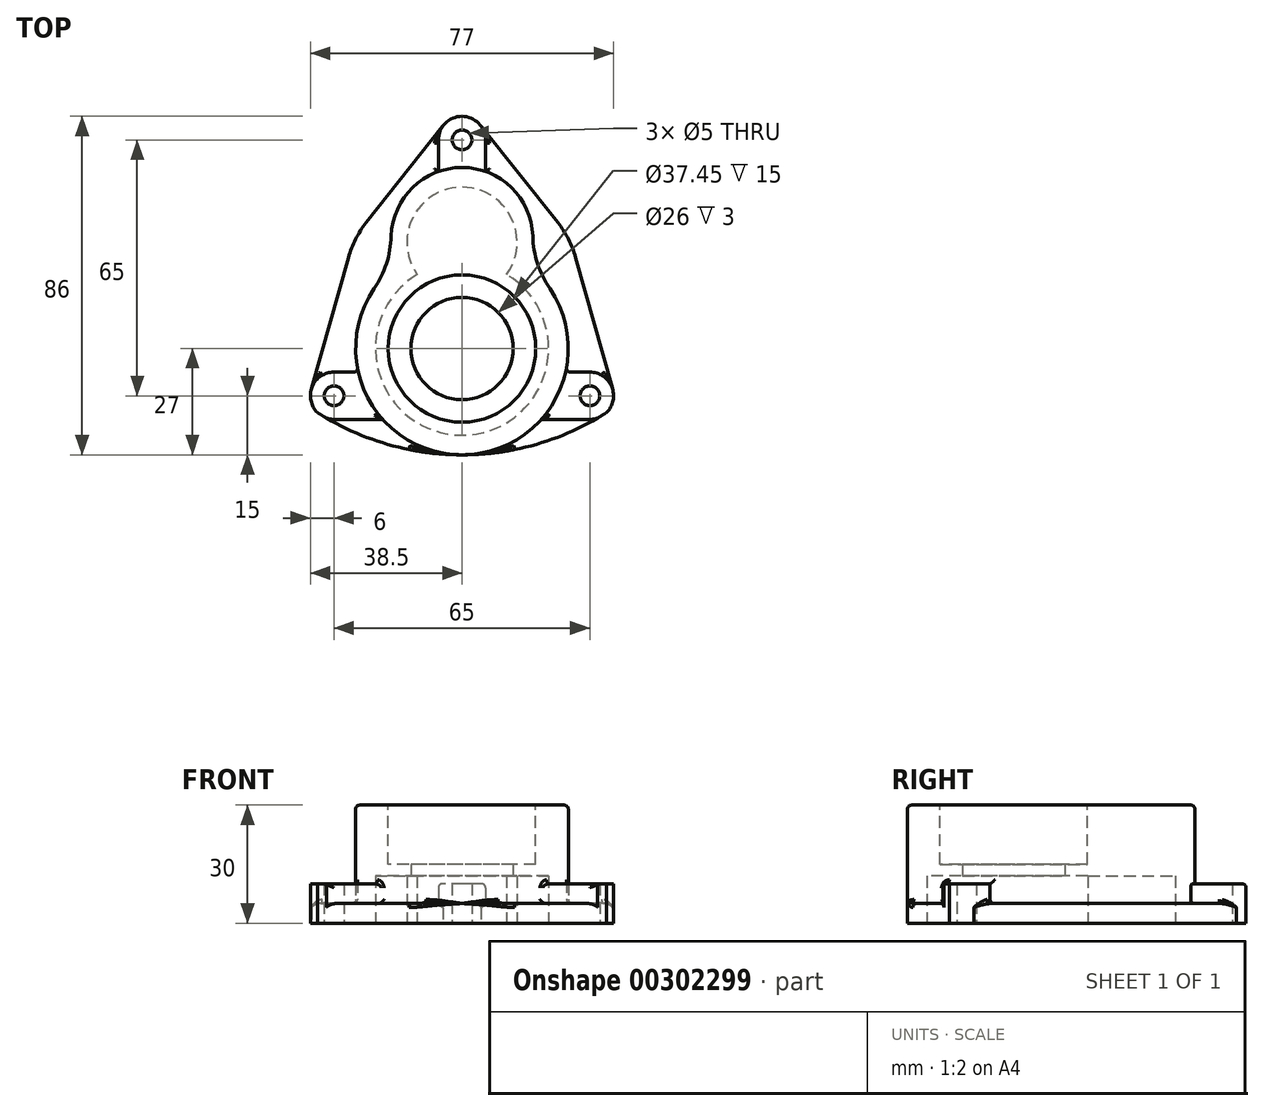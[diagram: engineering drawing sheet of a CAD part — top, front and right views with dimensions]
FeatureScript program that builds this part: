
annotation { "Feature Type Name" : "Feature", "Feature Type Description" : "" }
export const myFeature = defineFeature(function(context is Context, id is Id, definition is map)
    precondition{}
    {
        {
            var Q0;
            Q0=qCreatedBy(makeId("Top.planeOp"),FACE);
            var sketch = newSketch(context, id + "F0", { "sketchPlane" : qUnion([Q0])});
            skCircle(sketch, "E0", {"center": v(0, 0) * mm, "radius": 13 * mm});
            skCircle(sketch, "E1", {"center": v(0, 0) * mm, "radius": 22 * mm});
            skCircle(sketch, "E2", {"center": v(0, 53) * mm, "radius": 2.5 * mm});
            skCircle(sketch, "E3", {"center": v(0, 53) * mm, "radius": 6 * mm});
            skCircle(sketch, "E4", {"center": v(32.5, -12) * mm, "radius": 2.5 * mm});
            skCircle(sketch, "E5", {"center": v(32.5, -12) * mm, "radius": 6 * mm});
            skCircle(sketch, "E6", {"center": v(-32.5, -12) * mm, "radius": 2.5 * mm});
            skCircle(sketch, "E7", {"center": v(-32.5, -12) * mm, "radius": 6 * mm});
            skCircle(sketch, "E8", {"center": v(0, 27) * mm, "radius": 14 * mm});
            skLineSegment(sketch, "E9", {"start": v(32.5, -18) * mm, "end": v(20.12, -18) * mm});
            skLineSegment(sketch, "E10", {"start": v(32.5, -6) * mm, "end": v(26.32, -6) * mm});
            skLineSegment(sketch, "E11", {"start": v(-32.5, -6) * mm, "end": v(-26.32, -6) * mm});
            skLineSegment(sketch, "E12", {"start": v(-32.5, -18) * mm, "end": v(-20.12, -18) * mm});
            skLineSegment(sketch, "E13", {"start": v(-6, 53) * mm, "end": v(-6, 44.97) * mm});
            skLineSegment(sketch, "E14", {"start": v(6, 53) * mm, "end": v(6, 44.97) * mm});
            skLineSegment(sketch, "E15", {"start": v(4.87, 56.5) * mm, "end": v(24.37, 31.94) * mm});
            skLineSegment(sketch, "E16", {"start": v(-4.87, 56.5) * mm, "end": v(-24.37, 31.94) * mm});
            skLineSegment(sketch, "E17", {"start": v(-38.18, -10.07) * mm, "end": v(-28.86, 23.15) * mm});
            skLineSegment(sketch, "E18", {"start": v(38.18, -10.07) * mm, "end": v(28.86, 23.15) * mm});
            skArc(sketch, "E19", {"start": v(-36.7, -16.28) * mm, "mid": v(0, -27) * mm, "end": v(36.7, -16.28) * mm});
            skPoint(sketch, "E20.visualSharp", {"position": v(27.5, 28) * mm});
            skArc(sketch, "E20.filletArc", {"start": v(28.86, 23.15) * mm, "mid": v(27.05, 27.77) * mm, "end": v(24.37, 31.94) * mm});
            skPoint(sketch, "E21.visualSharp", {"position": v(-27.5, 28) * mm});
            skArc(sketch, "E21.filletArc", {"start": v(-24.37, 31.94) * mm, "mid": v(-27.05, 27.77) * mm, "end": v(-28.86, 23.15) * mm});
            skArc(sketch, "E22", {"start": v(16.68, 21.23) * mm, "mid": v(0, 46) * mm, "end": v(-16.68, 21.23) * mm});
            skArc(sketch, "E23", {"start": v(-16.68, 21.23) * mm, "mid": v(0, -27) * mm, "end": v(16.68, 21.23) * mm});
            skCircle(sketch, "E24", {"center": v(0, 0) * mm, "radius": 18.73 * mm});
            skSolve(sketch);
        }
        {
            var Q0;
            {var subQ3=sQuery(id+"F0.wireOp",EDGE,"E8");var subQ4=sQuery(id+"F0.wireOp",EDGE,"E1");var subQ5=makeQuery(id+"F0.imprint","INTERSECT",VERTEX,{"disambiguationData":[OD(0.0)],"derivedFrom":[subQ4,subQ3]});Q0=makeQuery(id+"F0.imprint","IMPRINT",FACE,{"disambiguationData":[TD([[makeQuery(id+"F0.imprint","IMPRINT",EDGE,{"disambiguationData":[TD([[subQ5,-1.0]])],"derivedFrom":subQ4}),-1.0]])]});}
            var Q1;
            {var subQ0=sQuery(id+"F0.wireOp",EDGE,"E8");var subQ1=sQuery(id+"F0.wireOp",EDGE,"E1");var subQ2=makeQuery(id+"F0.imprint","INTERSECT",VERTEX,{"disambiguationData":[OD(0.0)],"derivedFrom":[subQ1,subQ0]});Q1=makeQuery(id+"F0.imprint","IMPRINT",FACE,{"disambiguationData":[TD([[makeQuery(id+"F0.imprint","IMPRINT",EDGE,{"disambiguationData":[TD([[subQ2,1.0]])],"derivedFrom":subQ1}),-1.0]])]});}
            var Q2;
            {var subQ0=sQuery(id+"F0.wireOp",EDGE,"E8");var subQ1=sQuery(id+"F0.wireOp",EDGE,"E1");var subQ2=makeQuery(id+"F0.imprint","INTERSECT",VERTEX,{"disambiguationData":[OD(0.0)],"derivedFrom":[subQ1,subQ0]});Q2=makeQuery(id+"F0.imprint","IMPRINT",FACE,{"disambiguationData":[TD([[makeQuery(id+"F0.imprint","IMPRINT",EDGE,{"disambiguationData":[TD([[subQ2,1.0]])],"derivedFrom":subQ1}),1.0]])]});}
            var Q3;
            {var subQ0=sQuery(id+"F0.wireOp",EDGE,"E8");var subQ1=makeQuery(id+"F0.imprint","INTERSECT",VERTEX,{"derivedFrom":[sQuery(id+"F0.wireOp",EDGE,"E0"),subQ0]});Q3=makeQuery(id+"F0.imprint","IMPRINT",FACE,{"disambiguationData":[TD([[makeQuery(id+"F0.imprint","IMPRINT",EDGE,{"disambiguationData":[TD([[subQ1,1.0]])],"derivedFrom":subQ0}),1.0]])]});}
            var Q4;
            Q4=makeQuery(id+"F0.imprint","IMPRINT",FACE,{"disambiguationData":[TD([[makeQuery(id+"F0.imprint","IMPRINT",EDGE,{"derivedFrom":sQuery(id+"F0.wireOp",EDGE,"E0")}),1.0]])]});
            var Q5;
            {var subQ0=sQuery(id+"F0.wireOp",EDGE,"E0");Q5=makeQuery(id+"F0.imprint","IMPRINT",FACE,{"disambiguationData":[TD([[makeQuery(id+"F0.imprint","IMPRINT",EDGE,{"derivedFrom":subQ0}),-1.0]])]});}
            var Q6;
            {var subQ0=sQuery(id+"F0.wireOp",EDGE,"E8");var subQ1=sQuery(id+"F0.wireOp",EDGE,"E1");var subQ2=makeQuery(id+"F0.imprint","INTERSECT",VERTEX,{"disambiguationData":[OD(0.0)],"derivedFrom":[subQ1,subQ0]});Q6=makeQuery(id+"F0.imprint","IMPRINT",FACE,{"disambiguationData":[TD([[makeQuery(id+"F0.imprint","IMPRINT",EDGE,{"disambiguationData":[TD([[subQ2,-1.0]])],"derivedFrom":subQ1}),1.0]])]});}
            extrude(context, id + "F1", {"entities" : qUnion([Q0, Q1, Q2, Q3, Q4, Q5, Q6]), "depth" : 30 * mm});
        }
        {
            var Q0;
            Q0=makeQuery(id+"F0.imprint","IMPRINT",FACE,{"disambiguationData":[TD([[makeQuery(id+"F0.imprint","IMPRINT",EDGE,{"derivedFrom":sQuery(id+"F0.wireOp",EDGE,"E2")}),-1.0]])]});
            var Q1;
            {var subQ0=sQuery(id+"F0.wireOp",EDGE,"E13");Q1=makeQuery(id+"F0.imprint","IMPRINT",FACE,{"disambiguationData":[TD([[makeQuery(id+"F0.imprint","IMPRINT",EDGE,{"derivedFrom":subQ0}),1.0]])]});}
            var Q2;
            Q2=makeQuery(id+"F0.imprint","IMPRINT",FACE,{"disambiguationData":[TD([[makeQuery(id+"F0.imprint","IMPRINT",EDGE,{"derivedFrom":sQuery(id+"F0.wireOp",EDGE,"E4")}),-1.0]])]});
            var Q3;
            {var subQ0=sQuery(id+"F0.wireOp",EDGE,"E9");Q3=makeQuery(id+"F0.imprint","IMPRINT",FACE,{"disambiguationData":[TD([[makeQuery(id+"F0.imprint","IMPRINT",EDGE,{"derivedFrom":subQ0}),-1.0]])]});}
            var Q4;
            {var subQ0=sQuery(id+"F0.wireOp",EDGE,"E11");Q4=makeQuery(id+"F0.imprint","IMPRINT",FACE,{"disambiguationData":[TD([[makeQuery(id+"F0.imprint","IMPRINT",EDGE,{"derivedFrom":subQ0}),-1.0]])]});}
            var Q5;
            Q5=makeQuery(id+"F0.imprint","IMPRINT",FACE,{"disambiguationData":[TD([[makeQuery(id+"F0.imprint","IMPRINT",EDGE,{"derivedFrom":sQuery(id+"F0.wireOp",EDGE,"E6")}),-1.0]])]});
            extrude(context, id + "F2", {"entities" : qUnion([Q0, Q1, Q2, Q3, Q4, Q5]), "operationType" : NewBodyOperationType.ADD, "depth" : 10 * mm});
        }
        {
            var Q0;
            {var subQ1=sQuery(id+"F0.wireOp",EDGE,"E11");Q0=makeQuery(id+"F0.imprint","IMPRINT",FACE,{"disambiguationData":[TD([[makeQuery(id+"F0.imprint","IMPRINT",EDGE,{"derivedFrom":subQ1}),1.0]])]});}
            var Q1;
            {var subQ4=sQuery(id+"F0.wireOp",EDGE,"E10");Q1=makeQuery(id+"F0.imprint","IMPRINT",FACE,{"disambiguationData":[TD([[makeQuery(id+"F0.imprint","IMPRINT",EDGE,{"derivedFrom":subQ4}),-1.0]])]});}
            var Q2;
            {var subQ0=sQuery(id+"F0.wireOp",EDGE,"E9");Q2=makeQuery(id+"F0.imprint","IMPRINT",FACE,{"disambiguationData":[TD([[makeQuery(id+"F0.imprint","IMPRINT",EDGE,{"derivedFrom":subQ0}),1.0]])]});}
            var Q3;
            {var subQ0=sQuery(id+"F0.wireOp",EDGE,"E12");Q3=makeQuery(id+"F0.imprint","IMPRINT",FACE,{"disambiguationData":[TD([[makeQuery(id+"F0.imprint","IMPRINT",EDGE,{"derivedFrom":subQ0}),-1.0]])]});}
            extrude(context, id + "F3", {"entities" : qUnion([Q0, Q1, Q2, Q3]), "operationType" : NewBodyOperationType.ADD, "depth" : 5 * mm});
        }
        {
            var Q0;
            {var subQ0=sQuery(id+"F0.wireOp",EDGE,"E23");var subQ1=sQuery(id+"F0.wireOp",EDGE,"E22");Q0=makeQuery(id+"F1.opExtrude","SWEPT_EDGE",EDGE,{"disambiguationData":[OSD([subQ1,subQ0]),TDD([makeQuery(id+"F0.imprint","INTERSECT",VERTEX,{"disambiguationData":[OD(1.0)],"derivedFrom":[subQ1,subQ0]})])]});}
            var Q1;
            {var subQ0=sQuery(id+"F0.wireOp",EDGE,"E23");var subQ1=sQuery(id+"F0.wireOp",EDGE,"E22");Q1=makeQuery(id+"F1.opExtrude","SWEPT_EDGE",EDGE,{"disambiguationData":[OSD([subQ1,subQ0]),TDD([makeQuery(id+"F0.imprint","INTERSECT",VERTEX,{"disambiguationData":[OD(0.0)],"derivedFrom":[subQ1,subQ0]})])]});}
            fillet(context, id + "F4", {"entities" : qUnion([Q0, Q1]), "radius" : 25 * mm, "tangentPropagation" : true, "allowEdgeOverflow" : false});
        }
        {
            var Q0;
            {var subQ0=sQuery(id+"F0.wireOp",EDGE,"E8");var subQ1=sQuery(id+"F0.wireOp",EDGE,"E1");var subQ2=makeQuery(id+"F0.imprint","INTERSECT",VERTEX,{"disambiguationData":[OD(0.0)],"derivedFrom":[subQ1,subQ0]});Q0=makeQuery(id+"F0.imprint","IMPRINT",FACE,{"disambiguationData":[TD([[makeQuery(id+"F0.imprint","IMPRINT",EDGE,{"disambiguationData":[TD([[subQ2,1.0]])],"derivedFrom":subQ1}),-1.0]])]});}
            var Q1;
            {var subQ0=sQuery(id+"F0.wireOp",EDGE,"E8");var subQ1=sQuery(id+"F0.wireOp",EDGE,"E1");var subQ2=makeQuery(id+"F0.imprint","INTERSECT",VERTEX,{"disambiguationData":[OD(0.0)],"derivedFrom":[subQ1,subQ0]});Q1=makeQuery(id+"F0.imprint","IMPRINT",FACE,{"disambiguationData":[TD([[makeQuery(id+"F0.imprint","IMPRINT",EDGE,{"disambiguationData":[TD([[subQ2,1.0]])],"derivedFrom":subQ1}),1.0]])]});}
            var Q2;
            {var subQ0=sQuery(id+"F0.wireOp",EDGE,"E8");var subQ1=makeQuery(id+"F0.imprint","INTERSECT",VERTEX,{"derivedFrom":[sQuery(id+"F0.wireOp",EDGE,"E0"),subQ0]});Q2=makeQuery(id+"F0.imprint","IMPRINT",FACE,{"disambiguationData":[TD([[makeQuery(id+"F0.imprint","IMPRINT",EDGE,{"disambiguationData":[TD([[subQ1,1.0]])],"derivedFrom":subQ0}),1.0]])]});}
            var Q3;
            {var subQ0=sQuery(id+"F0.wireOp",EDGE,"E8");var subQ1=sQuery(id+"F0.wireOp",EDGE,"E1");var subQ2=makeQuery(id+"F0.imprint","INTERSECT",VERTEX,{"disambiguationData":[OD(0.0)],"derivedFrom":[subQ1,subQ0]});Q3=makeQuery(id+"F0.imprint","IMPRINT",FACE,{"disambiguationData":[TD([[makeQuery(id+"F0.imprint","IMPRINT",EDGE,{"disambiguationData":[TD([[subQ2,-1.0]])],"derivedFrom":subQ1}),1.0]])]});}
            var Q4;
            {var subQ0=sQuery(id+"F0.wireOp",EDGE,"E0");Q4=makeQuery(id+"F0.imprint","IMPRINT",FACE,{"disambiguationData":[TD([[makeQuery(id+"F0.imprint","IMPRINT",EDGE,{"derivedFrom":subQ0}),-1.0]])]});}
            var Q5;
            Q5=makeQuery(id+"F0.imprint","IMPRINT",FACE,{"disambiguationData":[TD([[makeQuery(id+"F0.imprint","IMPRINT",EDGE,{"derivedFrom":sQuery(id+"F0.wireOp",EDGE,"E0")}),1.0]])]});
            extrude(context, id + "F5", {"entities" : qUnion([Q0, Q1, Q2, Q3, Q4, Q5]), "operationType" : NewBodyOperationType.REMOVE, "depth" : 12 * mm});
        }
        {
            var Q0;
            Q0=makeQuery(id+"F1.opExtrude","CAP_FACE",FACE,{"disambiguationData":[OSD([sQuery(id+"F0.wireOp",EDGE,"E22"),sQuery(id+"F0.wireOp",EDGE,"E23")])],"isStart":false});
            var sketch = newSketch(context, id + "F6", { "sketchPlane" : qUnion([Q0])});
            skCircle(sketch, "E25.0", {"center": v(0, 0) * mm, "radius": 18.73 * mm});
            skSolve(sketch);
        }
        {
            var Q0;
            Q0 = qSketchRegion(id + "F6", true);
            extrude(context, id + "F7", {"entities" : qUnion([Q0]), "operationType" : NewBodyOperationType.REMOVE, "oppositeDirection" : true, "depth" : 15 * mm});
        }
        {
            var Q0;
            Q0=makeQuery(id+"F0.imprint","IMPRINT",FACE,{"disambiguationData":[TD([[makeQuery(id+"F0.imprint","IMPRINT",EDGE,{"derivedFrom":sQuery(id+"F0.wireOp",EDGE,"E0")}),1.0]])]});
            extrude(context, id + "F8", {"entities" : qUnion([Q0]), "operationType" : NewBodyOperationType.REMOVE, "endBound" : BoundingType.THROUGH_ALL, "depth" : 25 * mm});
        }
        {
            var Q0;
            Q0=makeQuery(id+"F1.opExtrude","SWEPT_FACE",FACE,{"disambiguationData":[OSD([sQuery(id+"F0.wireOp",EDGE,"E23")])]});
            var Q1;
            Q1=makeQuery(id+"F3.opExtrude","CAP_FACE",FACE,{"disambiguationData":[OSD([sQuery(id+"F0.wireOp",EDGE,"E3"),sQuery(id+"F0.wireOp",EDGE,"E5"),sQuery(id+"F0.wireOp",EDGE,"E10"),sQuery(id+"F0.wireOp",EDGE,"E14"),sQuery(id+"F0.wireOp",EDGE,"E15"),sQuery(id+"F0.wireOp",EDGE,"E18"),sQuery(id+"F0.wireOp",EDGE,"E20.filletArc"),sQuery(id+"F0.wireOp",EDGE,"E22"),sQuery(id+"F0.wireOp",EDGE,"E23")])],"isStart":false});
            var Q2;
            Q2=makeQuery(id+"F2.opExtrude","CAP_EDGE",EDGE,{"disambiguationData":[OSD([sQuery(id+"F0.wireOp",EDGE,"E14")])],"isStart":false});
            var Q3;
            Q3=makeQuery(id+"F3.opExtrude","CAP_FACE",FACE,{"disambiguationData":[OSD([sQuery(id+"F0.wireOp",EDGE,"E3"),sQuery(id+"F0.wireOp",EDGE,"E7"),sQuery(id+"F0.wireOp",EDGE,"E11"),sQuery(id+"F0.wireOp",EDGE,"E13"),sQuery(id+"F0.wireOp",EDGE,"E16"),sQuery(id+"F0.wireOp",EDGE,"E17"),sQuery(id+"F0.wireOp",EDGE,"E21.filletArc"),sQuery(id+"F0.wireOp",EDGE,"E22"),sQuery(id+"F0.wireOp",EDGE,"E23")])],"isStart":false});
            var Q4;
            Q4=makeQuery(id+"F2.opExtrude","CAP_EDGE",EDGE,{"disambiguationData":[OSD([sQuery(id+"F0.wireOp",EDGE,"E9")])],"isStart":false});
            var Q5;
            Q5=makeQuery(id+"F3.opExtrude","CAP_EDGE",EDGE,{"disambiguationData":[OSD([sQuery(id+"F0.wireOp",EDGE,"E9")])],"isStart":false});
            var Q6;
            Q6=makeQuery(id+"F2.opExtrude","CAP_EDGE",EDGE,{"disambiguationData":[OSD([sQuery(id+"F0.wireOp",EDGE,"E12")])],"isStart":false});
            var Q7;
            Q7=makeQuery(id+"F3.opExtrude","CAP_EDGE",EDGE,{"disambiguationData":[OSD([sQuery(id+"F0.wireOp",EDGE,"E12")])],"isStart":false});
            fillet(context, id + "F9", {"entities" : qUnion([Q0, Q1, Q2, Q3, Q4, Q5, Q6, Q7]), "radius" : 1 * mm, "tangentPropagation" : true, "allowEdgeOverflow" : false});
        }
        {
            var Q0;
            {var subQ0=sQuery(id+"F0.wireOp",EDGE,"E19");Q0=makeQuery(id+"F3.opExtrude","CAP_EDGE",EDGE,{"disambiguationData":[OSD([subQ0]),TDD([makeQuery(id+"F0.imprint","IMPRINT",EDGE,{"disambiguationData":[TD([[makeQuery(id+"F0.imprint","INTERSECT",VERTEX,{"disambiguationData":[OD(1.0)],"derivedFrom":[sQuery(id+"F0.wireOp",EDGE,"E7"),subQ0]}),-1.0]])],"derivedFrom":subQ0})])],"isStart":false});}
            var Q1;
            {var subQ0=sQuery(id+"F0.wireOp",EDGE,"E19");Q1=makeQuery(id+"F3.opExtrude","CAP_EDGE",EDGE,{"disambiguationData":[OSD([subQ0]),TDD([makeQuery(id+"F0.imprint","IMPRINT",EDGE,{"disambiguationData":[TD([[makeQuery(id+"F0.imprint","INTERSECT",VERTEX,{"disambiguationData":[OD(1.0)],"derivedFrom":[sQuery(id+"F0.wireOp",EDGE,"E5"),subQ0]}),1.0]])],"derivedFrom":subQ0})])],"isStart":false});}
            fillet(context, id + "F10", {"entities" : qUnion([Q0, Q1]), "radius" : 1 * mm, "tangentPropagation" : true, "allowEdgeOverflow" : false});
        }
    });
